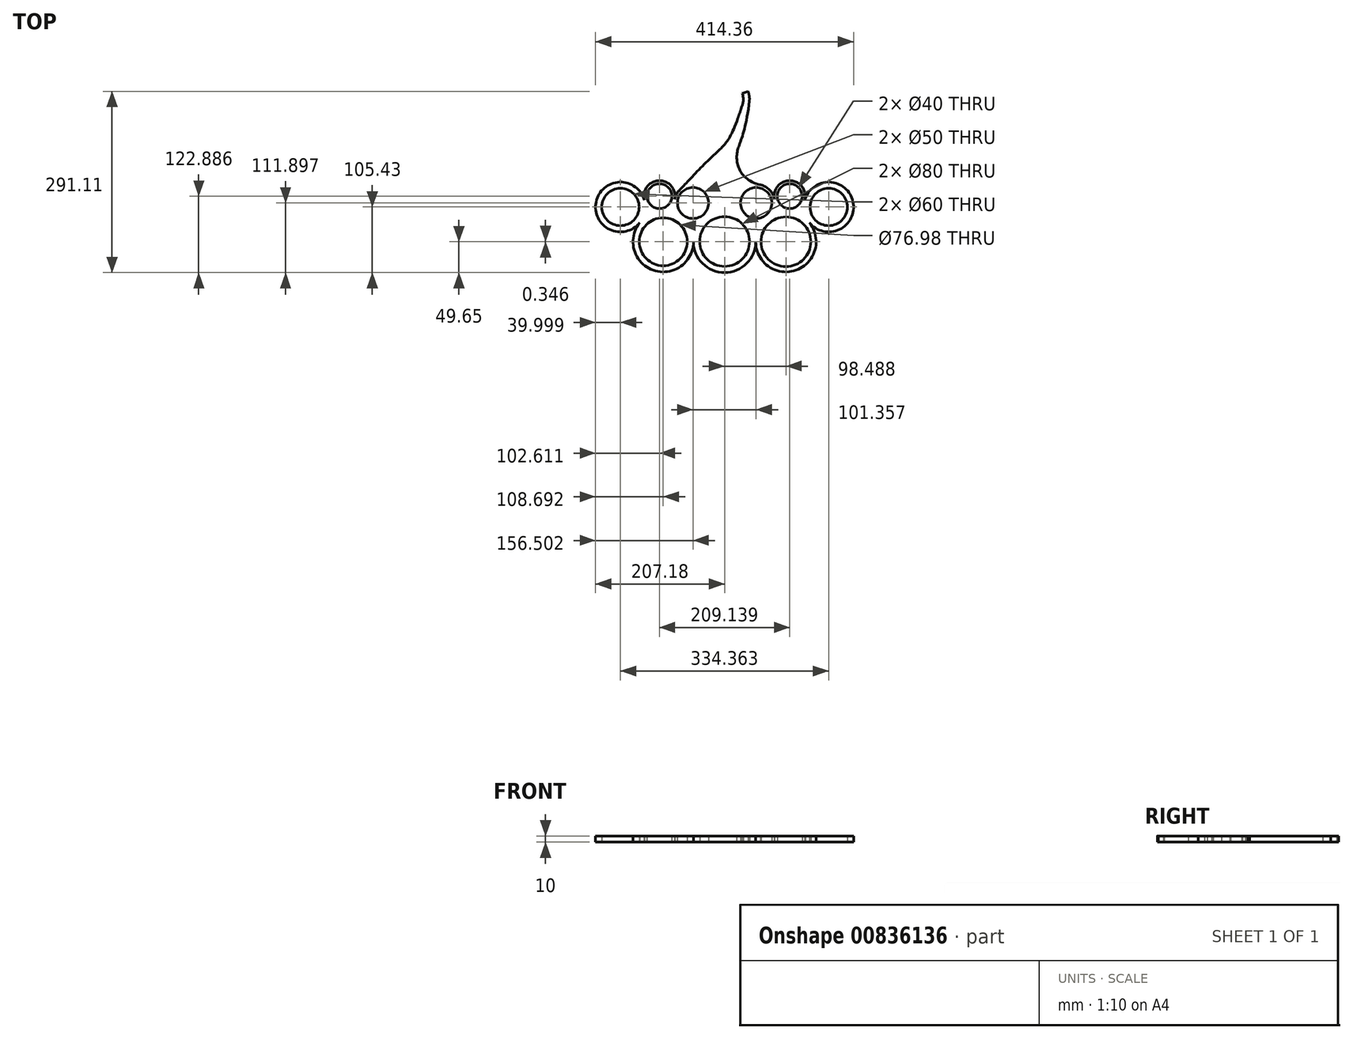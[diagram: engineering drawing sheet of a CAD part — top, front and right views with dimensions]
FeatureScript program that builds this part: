
annotation { "Feature Type Name" : "Feature", "Feature Type Description" : "" }
export const myFeature = defineFeature(function(context is Context, id is Id, definition is map)
    precondition{}
    {
        {
            var Q0;
            Q0=qCreatedBy(makeId("Top.planeOp"),FACE);
            var sketch = newSketch(context, id + "F0", { "sketchPlane" : qUnion([Q0])});
            skCircle(sketch, "E0", {"center": v(0, -55.43) * mm, "radius": 50 * mm});
            skCircle(sketch, "E1.0", {"center": v(0, -55.43) * mm, "radius": 40 * mm});
            skCircle(sketch, "E2.0.1.0", {"center": v(98.49, -55.78) * mm, "radius": 48.49 * mm});
            skCircle(sketch, "E2.2.1.0", {"center": v(98.49, -55.78) * mm, "radius": 40 * mm});
            skCircle(sketch, "E3.1.0.0", {"center": v(-98.49, -55.78) * mm, "radius": 48.49 * mm});
            skCircle(sketch, "E4.0", {"center": v(-98.49, -55.78) * mm, "radius": 38.49 * mm});
            skLineSegment(sketch, "E5.bottom", {"start": v(-19.58, 81.56) * mm, "end": v(19.58, 81.56) * mm});
            skLineSegment(sketch, "E5.top", {"start": v(-19.58, -5.43) * mm, "end": v(19.58, -5.43) * mm});
            skLineSegment(sketch, "E5.left", {"start": v(-19.58, 81.56) * mm, "end": v(-19.58, -5.43) * mm});
            skLineSegment(sketch, "E5.right", {"start": v(19.58, 81.56) * mm, "end": v(19.58, -5.43) * mm});
            skPoint(sketch, "E5.middle", {"position": v(0, 38.06) * mm});
            skCircle(sketch, "E6", {"center": v(-50.68, 6.47) * mm, "radius": 30 * mm});
            skCircle(sketch, "E7", {"center": v(50.68, 6.47) * mm, "radius": 30 * mm});
            skCircle(sketch, "E8", {"center": v(0, 172.8) * mm, "radius": 40 * mm});
            skFitSpline(sketch, "E9", {"points": [v(40, 172.8) * mm, v(19.58, 81.56) * mm, v(57.59, 35.66) * mm], "startDerivative": vector(-34.66, -337.72) * mm, "endDerivative": vector(209.1, -46.05) * mm});
            skCircle(sketch, "E10.0", {"center": v(0, 172.8) * mm, "radius": 30 * mm});
            skFitSpline(sketch, "E11", {"points": [v(27.12, 159.99) * mm, v(-19.58, 81.56) * mm, v(-71.38, 28.18) * mm, v(-72.3, 27.26) * mm], "startDerivative": vector(-109.12, -345.48) * mm, "endDerivative": vector(-8.77, -9.29) * mm});
            skLineSegment(sketch, "E12", {"start": v(-37.93, 160.11) * mm, "end": v(37.87, 185.68) * mm});
            skCircle(sketch, "E13", {"center": v(-104.57, 17.46) * mm, "radius": 25 * mm});
            skCircle(sketch, "E14", {"center": v(104.57, 17.46) * mm, "radius": 25 * mm});
            skCircle(sketch, "E15", {"center": v(-167.18, 0) * mm, "radius": 40 * mm});
            skCircle(sketch, "E16", {"center": v(167.18, 0) * mm, "radius": 40 * mm});
            skCircle(sketch, "E17.0", {"center": v(-167.18, 0) * mm, "radius": 30 * mm});
            skCircle(sketch, "E18.0", {"center": v(167.18, 0) * mm, "radius": 30 * mm});
            skCircle(sketch, "E19.0", {"center": v(-104.57, 17.46) * mm, "radius": 20 * mm});
            skCircle(sketch, "E20.0", {"center": v(-50.68, 6.47) * mm, "radius": 25 * mm});
            skCircle(sketch, "E21.0", {"center": v(50.68, 6.47) * mm, "radius": 25 * mm});
            skCircle(sketch, "E22.0", {"center": v(104.57, 17.46) * mm, "radius": 20 * mm});
            skSolve(sketch);
        }
        {
            var Q0;
            {var subQ5=sQuery(id+"F0.wireOp",EDGE,"E8");var subQ7=sQuery(id+"F0.wireOp",EDGE,"E9");var subQ9=makeQuery(id+"F0.imprint","INTERSECT",VERTEX,{"disambiguationData":[OD(0.0)],"derivedFrom":[subQ5,subQ7]});Q0=makeQuery(id+"F0.imprint","IMPRINT",FACE,{"disambiguationData":[TD([[makeQuery(id+"F0.imprint","IMPRINT",EDGE,{"disambiguationData":[TD([[subQ9,-1.0]])],"derivedFrom":subQ5}),1.0]])]});}
            var Q1;
            {var subQ0=sQuery(id+"F0.wireOp",EDGE,"E12");var subQ1=sQuery(id+"F0.wireOp",EDGE,"E8");var subQ2=makeQuery(id+"F0.imprint","INTERSECT",VERTEX,{"disambiguationData":[OD(0.0)],"derivedFrom":[subQ1,subQ0]});Q1=makeQuery(id+"F0.imprint","IMPRINT",FACE,{"disambiguationData":[TD([[makeQuery(id+"F0.imprint","IMPRINT",EDGE,{"disambiguationData":[TD([[subQ2,1.0]])],"derivedFrom":subQ1}),1.0]])]});}
            var Q2;
            {var subQ0=sQuery(id+"F0.wireOp",EDGE,"E5.bottom");Q2=makeQuery(id+"F0.imprint","IMPRINT",FACE,{"disambiguationData":[TD([[makeQuery(id+"F0.imprint","IMPRINT",EDGE,{"derivedFrom":subQ0}),1.0]])]});}
            var Q3;
            {var subQ0=sQuery(id+"F0.wireOp",EDGE,"E5.left");Q3=makeQuery(id+"F0.imprint","IMPRINT",FACE,{"disambiguationData":[TD([[makeQuery(id+"F0.imprint","IMPRINT",EDGE,{"derivedFrom":subQ0}),-1.0]])]});}
            var Q4;
            {var subQ6=sQuery(id+"F0.wireOp",EDGE,"E5.bottom");Q4=makeQuery(id+"F0.imprint","IMPRINT",FACE,{"disambiguationData":[TD([[makeQuery(id+"F0.imprint","IMPRINT",EDGE,{"derivedFrom":subQ6}),-1.0]])]});}
            var Q5;
            {var subQ3=sQuery(id+"F0.wireOp",EDGE,"E0");var subQ6=sQuery(id+"F0.wireOp",EDGE,"E5.top");var subQ8=makeQuery(id+"F0.imprint","INTERSECT",VERTEX,{"derivedFrom":[subQ3,subQ6]});Q5=makeQuery(id+"F0.imprint","IMPRINT",FACE,{"disambiguationData":[TD([[makeQuery(id+"F0.imprint","IMPRINT",EDGE,{"disambiguationData":[TD([[subQ8,1.0]])],"derivedFrom":subQ3}),-1.0]])]});}
            var Q6;
            Q6=makeQuery(id+"F0.imprint","IMPRINT",FACE,{"disambiguationData":[TD([[makeQuery(id+"F0.imprint","IMPRINT",EDGE,{"derivedFrom":sQuery(id+"F0.wireOp",EDGE,"E21.0")}),-1.0]])]});
            var Q7;
            Q7=makeQuery(id+"F0.imprint","IMPRINT",FACE,{"disambiguationData":[TD([[makeQuery(id+"F0.imprint","IMPRINT",EDGE,{"derivedFrom":sQuery(id+"F0.wireOp",EDGE,"E22.0")}),-1.0]])]});
            var Q8;
            Q8=makeQuery(id+"F0.imprint","IMPRINT",FACE,{"disambiguationData":[TD([[makeQuery(id+"F0.imprint","IMPRINT",EDGE,{"derivedFrom":sQuery(id+"F0.wireOp",EDGE,"E18.0")}),-1.0]])]});
            var Q9;
            {var subQ0=sQuery(id+"F0.wireOp",EDGE,"E14");var subQ1=sQuery(id+"F0.wireOp",EDGE,"E2.0.1.0");var subQ2=makeQuery(id+"F0.imprint","INTERSECT",VERTEX,{"derivedFrom":[subQ1,subQ0]});Q9=makeQuery(id+"F0.imprint","IMPRINT",FACE,{"disambiguationData":[TD([[makeQuery(id+"F0.imprint","IMPRINT",EDGE,{"disambiguationData":[TD([[subQ2,-1.0]])],"derivedFrom":subQ1}),-1.0]])]});}
            var Q10;
            {var subQ0=sQuery(id+"F0.wireOp",EDGE,"E16");var subQ1=sQuery(id+"F0.wireOp",EDGE,"E2.0.1.0");var subQ2=makeQuery(id+"F0.imprint","INTERSECT",VERTEX,{"derivedFrom":[subQ1,subQ0]});Q10=makeQuery(id+"F0.imprint","IMPRINT",FACE,{"disambiguationData":[TD([[makeQuery(id+"F0.imprint","IMPRINT",EDGE,{"disambiguationData":[TD([[subQ2,-1.0]])],"derivedFrom":subQ1}),-1.0]])]});}
            var Q11;
            Q11=makeQuery(id+"F0.imprint","IMPRINT",FACE,{"disambiguationData":[TD([[makeQuery(id+"F0.imprint","IMPRINT",EDGE,{"derivedFrom":sQuery(id+"F0.wireOp",EDGE,"E2.2.1.0")}),-1.0]])]});
            var Q12;
            {var subQ0=sQuery(id+"F0.wireOp",EDGE,"E2.0.1.0");var subQ1=sQuery(id+"F0.wireOp",EDGE,"E0");var subQ2=makeQuery(id+"F0.imprint","INTERSECT",VERTEX,{"derivedFrom":[subQ1,subQ0]});Q12=makeQuery(id+"F0.imprint","IMPRINT",FACE,{"disambiguationData":[TD([[makeQuery(id+"F0.imprint","IMPRINT",EDGE,{"disambiguationData":[TD([[subQ2,-1.0]])],"derivedFrom":subQ1}),-1.0]])]});}
            var Q13;
            Q13=makeQuery(id+"F0.imprint","IMPRINT",FACE,{"disambiguationData":[TD([[makeQuery(id+"F0.imprint","IMPRINT",EDGE,{"derivedFrom":sQuery(id+"F0.wireOp",EDGE,"E1.0")}),-1.0]])]});
            var Q14;
            Q14=makeQuery(id+"F0.imprint","IMPRINT",FACE,{"disambiguationData":[TD([[makeQuery(id+"F0.imprint","IMPRINT",EDGE,{"derivedFrom":sQuery(id+"F0.wireOp",EDGE,"E4.0")}),-1.0]])]});
            var Q15;
            {var subQ0=sQuery(id+"F0.wireOp",EDGE,"E3.1.0.0");var subQ1=sQuery(id+"F0.wireOp",EDGE,"E0");var subQ2=makeQuery(id+"F0.imprint","INTERSECT",VERTEX,{"derivedFrom":[subQ1,subQ0]});Q15=makeQuery(id+"F0.imprint","IMPRINT",FACE,{"disambiguationData":[TD([[makeQuery(id+"F0.imprint","IMPRINT",EDGE,{"disambiguationData":[TD([[subQ2,1.0]])],"derivedFrom":subQ1}),-1.0]])]});}
            var Q16;
            Q16=makeQuery(id+"F0.imprint","IMPRINT",FACE,{"disambiguationData":[TD([[makeQuery(id+"F0.imprint","IMPRINT",EDGE,{"derivedFrom":sQuery(id+"F0.wireOp",EDGE,"E20.0")}),-1.0]])]});
            var Q17;
            {var subQ0=sQuery(id+"F0.wireOp",EDGE,"E6");var subQ1=sQuery(id+"F0.wireOp",EDGE,"E3.1.0.0");var subQ2=makeQuery(id+"F0.imprint","INTERSECT",VERTEX,{"derivedFrom":[subQ1,subQ0]});Q17=makeQuery(id+"F0.imprint","IMPRINT",FACE,{"disambiguationData":[TD([[makeQuery(id+"F0.imprint","IMPRINT",EDGE,{"disambiguationData":[TD([[subQ2,-1.0]])],"derivedFrom":subQ1}),-1.0]])]});}
            var Q18;
            Q18=makeQuery(id+"F0.imprint","IMPRINT",FACE,{"disambiguationData":[TD([[makeQuery(id+"F0.imprint","IMPRINT",EDGE,{"derivedFrom":sQuery(id+"F0.wireOp",EDGE,"E19.0")}),-1.0]])]});
            var Q19;
            {var subQ0=sQuery(id+"F0.wireOp",EDGE,"E15");var subQ1=sQuery(id+"F0.wireOp",EDGE,"E3.1.0.0");var subQ2=makeQuery(id+"F0.imprint","INTERSECT",VERTEX,{"derivedFrom":[subQ1,subQ0]});Q19=makeQuery(id+"F0.imprint","IMPRINT",FACE,{"disambiguationData":[TD([[makeQuery(id+"F0.imprint","IMPRINT",EDGE,{"disambiguationData":[TD([[subQ2,1.0]])],"derivedFrom":subQ1}),-1.0]])]});}
            var Q20;
            Q20=makeQuery(id+"F0.imprint","IMPRINT",FACE,{"disambiguationData":[TD([[makeQuery(id+"F0.imprint","IMPRINT",EDGE,{"derivedFrom":sQuery(id+"F0.wireOp",EDGE,"E17.0")}),-1.0]])]});
            extrude(context, id + "F1", {"entities" : qUnion([Q0, Q1, Q2, Q3, Q4, Q5, Q6, Q7, Q8, Q9, Q10, Q11, Q12, Q13, Q14, Q15, Q16, Q17, Q18, Q19, Q20]), "depth" : 10 * mm, "offsetDistance" : 25 * mm});
        }
    });
